FCSTD DOCUMENT  (FreeCAD 0.18R4 (GitTag))
Label: arm
License: All rights reserved
LicenseURL: http://en.wikipedia.org/wiki/All_rights_reserved
objects: Sketcher::SketchObject×1
note: 1 computed .brp shape members not serialized (recipe doc carries the construction recipe); baked Part::Feature solids carry a one-line shape summary decoded from their .brp

FEATURE [Sketcher::SketchObject] Sketch  label="Arm Holder"
  sketch-geometry (10):
    g0: LineSegment StartX=-15.5 StartY=25 StartZ=0 EndX=15.5 EndY=25 EndZ=0
    g1: LineSegment StartX=15.5 StartY=25 StartZ=0 EndX=15.5 EndY=-25 EndZ=0
    g2: LineSegment StartX=15.5 StartY=-25 StartZ=0 EndX=-14.9873 EndY=-24.9793 EndZ=0
    g3: LineSegment StartX=-14.9873 StartY=-24.9793 StartZ=0 EndX=-15.5 EndY=25 EndZ=0
    g4: Circle CenterX=-0.010938 CenterY=7.45508 CenterZ=0 NormalX=0 NormalY=0 NormalZ=1 AngleXU=0 Radius=1
    g5: Circle CenterX=0.003591 CenterY=-16.2778 CenterZ=0 NormalX=0 NormalY=0 NormalZ=1 AngleXU=0 Radius=2
    g6: LineSegment StartX=-11.55 StartY=6.15 StartZ=0 EndX=11.55 EndY=6.15 EndZ=0
    g7: LineSegment StartX=11.55 StartY=6.15 StartZ=0 EndX=11.55 EndY=-6.15 EndZ=0
    g8: LineSegment StartX=11.55 StartY=-6.15 StartZ=0 EndX=-11.55 EndY=-6.15 EndZ=0
    g9: LineSegment StartX=-11.55 StartY=-6.15 StartZ=0 EndX=-11.55 EndY=6.15 EndZ=0
  constraints (22):
    c: Coincident(g0,g1)
    c: Coincident(g1,g2)
    c: Coincident(g2,g3)
    c: Coincident(g3,g0)
    c: Symmetric(g1,g0,g-1)
    c: Symmetric(g0,g0,g-2)
    c: DistanceX(g0,g0) = 31
    c: DistanceY(g1,g1) = 50
    c: Coincident(g6,g7)
    c: Coincident(g7,g8)
    c: Coincident(g8,g9)
    c: Coincident(g9,g6)
    c: Horizontal(g6)
    c: Horizontal(g8)
    c: Vertical(g7)
    c: Vertical(g9)
    c: Radius(g5) = 2
    c: Radius(g4) = 1
    c: DistanceX(g8,g8) = 23.1
    c: DistanceY(g7,g7) = 12.3
    c: Symmetric(g6,g7,g-1)
    c: Symmetric(g6,g6,g-2)
